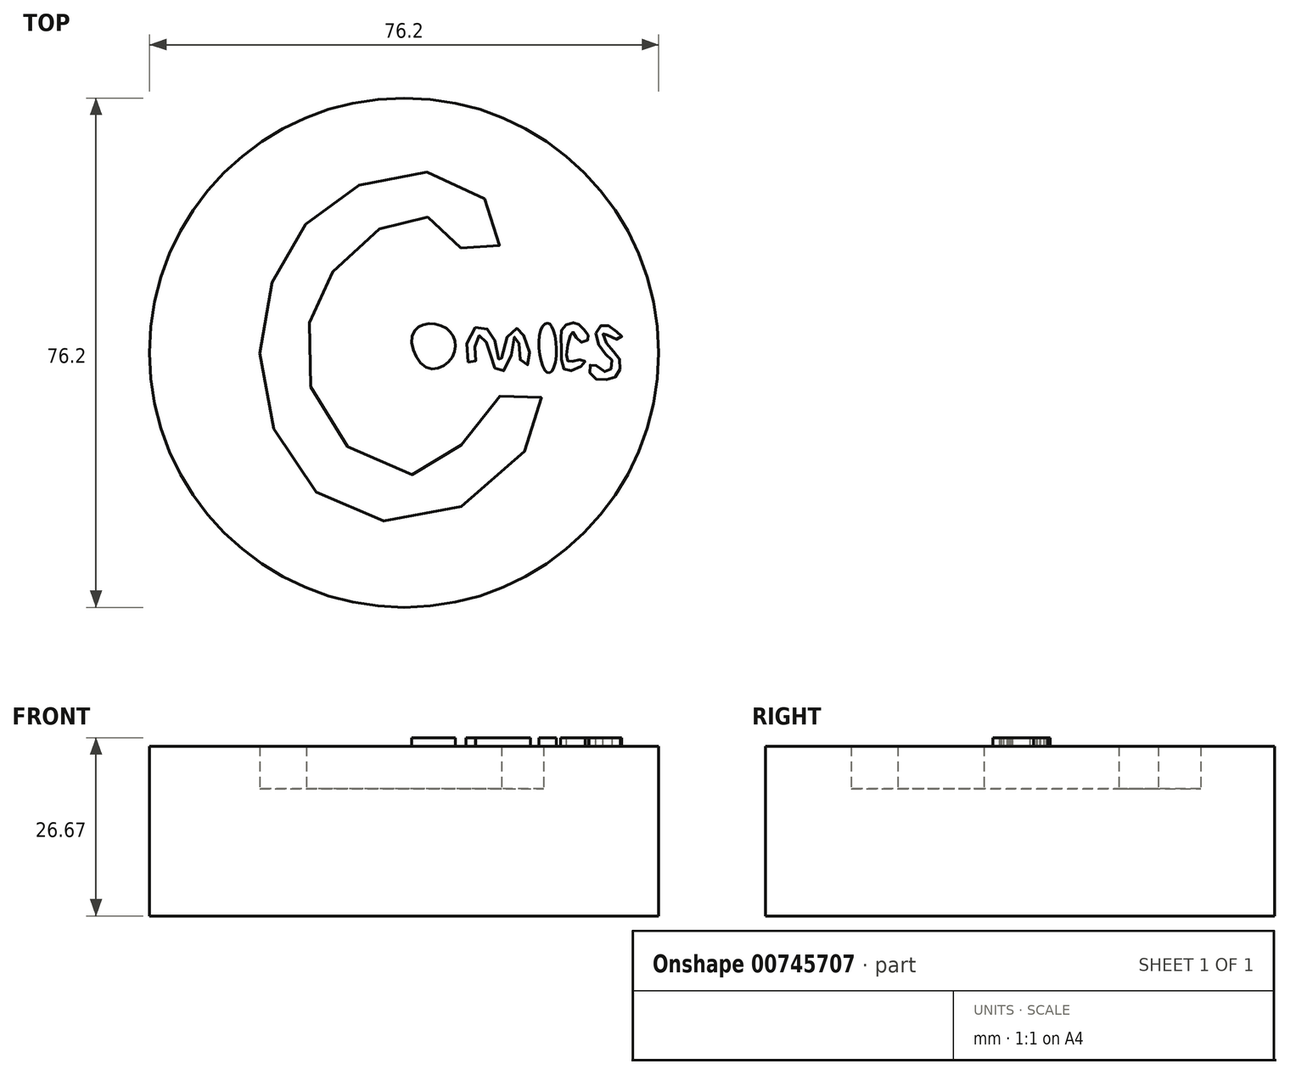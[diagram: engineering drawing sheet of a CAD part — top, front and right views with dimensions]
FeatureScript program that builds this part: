
annotation { "Feature Type Name" : "Feature", "Feature Type Description" : "" }
export const myFeature = defineFeature(function(context is Context, id is Id, definition is map)
    precondition{}
    {
        {
            var Q0;
            Q0=qCreatedBy(makeId("Top.planeOp"),FACE);
            var sketch = newSketch(context, id + "F0", { "sketchPlane" : qUnion([Q0])});
            skCircle(sketch, "E0", {"center": v(0, 0) * mm, "radius": 38.1 * mm});
            skSolve(sketch);
        }
        {
            var Q0;
            Q0=makeQuery(id+"F0.imprint","IMPRINT",FACE,{"disambiguationData":[TD([[makeQuery(id+"F0.imprint","IMPRINT",EDGE,{"derivedFrom":sQuery(id+"F0.wireOp",EDGE,"E0")}),1.0]])]});
            extrude(context, id + "F1", {"entities" : qUnion([Q0]), "depth" : 19.05 * mm, "offsetDistance" : 25.4 * mm});
        }
        {
            var Q0;
            Q0=makeQuery(id+"F1.opExtrude","CAP_FACE",FACE,{"disambiguationData":[OSD([sQuery(id+"F0.wireOp",EDGE,"E0")])],"isStart":false});
            var sketch = newSketch(context, id + "F2", { "sketchPlane" : qUnion([Q0])});
            skFitSpline(sketch, "E1", {"points": [v(8.5, 15.69) * mm, v(14.25, 15.97) * mm, v(9.93, 24.9) * mm, v(-6.48, 25.18) * mm, v(-18.28, 13.96) * mm, v(-21.15, -5.32) * mm, v(-9.93, -23.17) * mm, v(11.66, -21.15) * mm, v(20.58, -6.76) * mm, v(13.96, -6.76) * mm, v(4.46, -17.7) * mm, v(-10.8, -11.66) * mm, v(-14.25, 4.17) * mm, v(-8.2, 14.82) * mm, v(2.73, 20.58) * mm, v(8.5, 15.69) * mm]});
            skSolve(sketch);
        }
        {
            var Q0;
            Q0=makeQuery(id+"F2.imprint","IMPRINT",FACE,{"disambiguationData":[TD([[makeQuery(id+"F2.imprint","IMPRINT",EDGE,{"derivedFrom":sQuery(id+"F2.wireOp",EDGE,"E1")}),-1.0]])]});
            var sketch = newSketch(context, id + "F3", { "sketchPlane" : qUnion([Q0])});
            skFitSpline(sketch, "E2", {"points": [v(2.87, 4.2) * mm, v(1.14, 1.95) * mm, v(3.38, -2.22) * mm, v(6.73, -1.3) * mm, v(7.65, 1.55) * mm, v(6.22, 3.68) * mm, v(2.87, 4.2) * mm]});
            skSolve(sketch);
        }
        {
            var Q0;
            Q0=makeQuery(id+"F2.imprint","IMPRINT",FACE,{"disambiguationData":[TD([[makeQuery(id+"F2.imprint","IMPRINT",EDGE,{"derivedFrom":sQuery(id+"F2.wireOp",EDGE,"E1")}),-1.0]])]});
            var sketch = newSketch(context, id + "F4", { "sketchPlane" : qUnion([Q0])});
            skFitSpline(sketch, "E3", {"points": [v(9.58, -1.4) * mm, v(10.2, 3.38) * mm, v(12.23, 3.68) * mm, v(13.65, 1.55) * mm, v(14.37, -1.5) * mm, v(15.59, 2.67) * mm, v(17.11, 3.58) * mm, v(18.13, 1.95) * mm, v(18.74, -1.6) * mm, v(17.62, -1.7) * mm, v(17.21, 1.34) * mm, v(16.6, 2.46) * mm, v(15.59, -1.91) * mm, v(14.06, -2.83) * mm, v(13.04, -0.9) * mm, v(12.33, 1.55) * mm, v(11.31, 2.56) * mm, v(10.6, 0.94) * mm, v(10.6, -1.5) * mm, v(9.58, -1.4) * mm]});
            skSolve(sketch);
        }
        {
            var Q0;
            Q0=makeQuery(id+"F2.imprint","IMPRINT",FACE,{"disambiguationData":[TD([[makeQuery(id+"F2.imprint","IMPRINT",EDGE,{"derivedFrom":sQuery(id+"F2.wireOp",EDGE,"E1")}),-1.0]])]});
            var sketch = newSketch(context, id + "F5", { "sketchPlane" : qUnion([Q0])});
            skFitSpline(sketch, "E4", {"points": [v(20.47, -1.2) * mm, v(20.47, 3.48) * mm, v(21.49, 4.4) * mm, v(22.3, 3.48) * mm, v(22.6, -1.6) * mm, v(21.59, -3.03) * mm, v(20.47, -1.2) * mm]});
            skSolve(sketch);
        }
        {
            var Q0;
            Q0=makeQuery(id+"F2.imprint","IMPRINT",FACE,{"disambiguationData":[TD([[makeQuery(id+"F2.imprint","IMPRINT",EDGE,{"derivedFrom":sQuery(id+"F2.wireOp",EDGE,"E1")}),-1.0]])]});
            var sketch = newSketch(context, id + "F6", { "sketchPlane" : qUnion([Q0])});
            skFitSpline(sketch, "E5", {"points": [v(26.88, 3.48) * mm, v(25.56, 4.5) * mm, v(23.73, 3.68) * mm, v(23.52, 0.83) * mm, v(24.34, -2.73) * mm, v(27.08, -1.4) * mm, v(25.97, -1.1) * mm, v(24.54, -1.3) * mm, v(24.54, 1.24) * mm, v(25.25, 3.07) * mm, v(26.27, 1.65) * mm, v(27.6, 2.06) * mm, v(26.88, 3.48) * mm]});
            skSolve(sketch);
        }
        {
            var Q0;
            Q0=makeQuery(id+"F2.imprint","IMPRINT",FACE,{"disambiguationData":[TD([[makeQuery(id+"F2.imprint","IMPRINT",EDGE,{"derivedFrom":sQuery(id+"F2.wireOp",EDGE,"E1")}),-1.0]])]});
            var sketch = newSketch(context, id + "F7", { "sketchPlane" : qUnion([Q0])});
            skFitSpline(sketch, "E6", {"points": [v(31.77, 3.17) * mm, v(30.04, 4.2) * mm, v(28.71, 3.07) * mm, v(29.93, 0) * mm, v(31.15, -1.3) * mm, v(30.44, -2.93) * mm, v(28.61, -1.81) * mm, v(27.8, -1.91) * mm, v(28.1, -3.54) * mm, v(30.34, -4.05) * mm, v(32.07, -3.13) * mm, v(32.17, -0.8) * mm, v(30.44, 1.14) * mm, v(29.83, 2.97) * mm, v(31.36, 2.06) * mm, v(32.58, 2.36) * mm, v(31.77, 3.17) * mm]});
            skSolve(sketch);
        }
        {
            var Q0;
            Q0=makeQuery(id+"F2.imprint","IMPRINT",FACE,{"disambiguationData":[TD([[makeQuery(id+"F2.imprint","IMPRINT",EDGE,{"derivedFrom":sQuery(id+"F2.wireOp",EDGE,"E1")}),-1.0]])]});
            var Q1;
            Q1=makeQuery(id+"F3.imprint","IMPRINT",FACE,{"disambiguationData":[TD([[makeQuery(id+"F3.imprint","IMPRINT",EDGE,{"derivedFrom":sQuery(id+"F3.wireOp",EDGE,"E2")}),1.0]])]});
            var Q2;
            Q2=makeQuery(id+"F5.imprint","IMPRINT",FACE,{"disambiguationData":[TD([[makeQuery(id+"F5.imprint","IMPRINT",EDGE,{"derivedFrom":sQuery(id+"F5.wireOp",EDGE,"E4")}),-1.0]])]});
            var Q3;
            Q3=makeQuery(id+"F4.imprint","IMPRINT",FACE,{"disambiguationData":[TD([[makeQuery(id+"F4.imprint","IMPRINT",EDGE,{"derivedFrom":sQuery(id+"F4.wireOp",EDGE,"E3")}),-1.0]])]});
            var Q4;
            Q4=makeQuery(id+"F6.imprint","IMPRINT",FACE,{"disambiguationData":[TD([[makeQuery(id+"F6.imprint","IMPRINT",EDGE,{"derivedFrom":sQuery(id+"F6.wireOp",EDGE,"E5")}),1.0]])]});
            var Q5;
            Q5=makeQuery(id+"F7.imprint","IMPRINT",FACE,{"disambiguationData":[TD([[makeQuery(id+"F7.imprint","IMPRINT",EDGE,{"derivedFrom":sQuery(id+"F7.wireOp",EDGE,"E6")}),1.0]])]});
            extrude(context, id + "F8", {"entities" : qUnion([Q0, Q1, Q2, Q3, Q4, Q5]), "operationType" : NewBodyOperationType.ADD, "depth" : 6.35 * mm, "offsetDistance" : 25.4 * mm});
        }
        {
            var Q0;
            Q0 = qSketchRegion(id + "F4", true);
            extrude(context, id + "F9", {"entities" : qUnion([Q0]), "operationType" : NewBodyOperationType.ADD, "depth" : 7.62 * mm, "offsetDistance" : 25.4 * mm});
        }
        {
            var Q0;
            Q0 = qSketchRegion(id + "F3", true);
            extrude(context, id + "F10", {"entities" : qUnion([Q0]), "operationType" : NewBodyOperationType.ADD, "depth" : 7.62 * mm, "offsetDistance" : 25.4 * mm});
        }
        {
            var Q0;
            Q0 = qSketchRegion(id + "F5", true);
            extrude(context, id + "F11", {"entities" : qUnion([Q0]), "operationType" : NewBodyOperationType.ADD, "depth" : 7.62 * mm, "offsetDistance" : 25.4 * mm});
        }
        {
            var Q0;
            Q0 = qSketchRegion(id + "F6", true);
            extrude(context, id + "F12", {"entities" : qUnion([Q0]), "operationType" : NewBodyOperationType.ADD, "depth" : 7.62 * mm, "offsetDistance" : 25.4 * mm});
        }
        {
            var Q0;
            Q0 = qSketchRegion(id + "F7", true);
            extrude(context, id + "F13", {"entities" : qUnion([Q0]), "operationType" : NewBodyOperationType.ADD, "depth" : 7.62 * mm, "offsetDistance" : 25.4 * mm});
        }
    });
